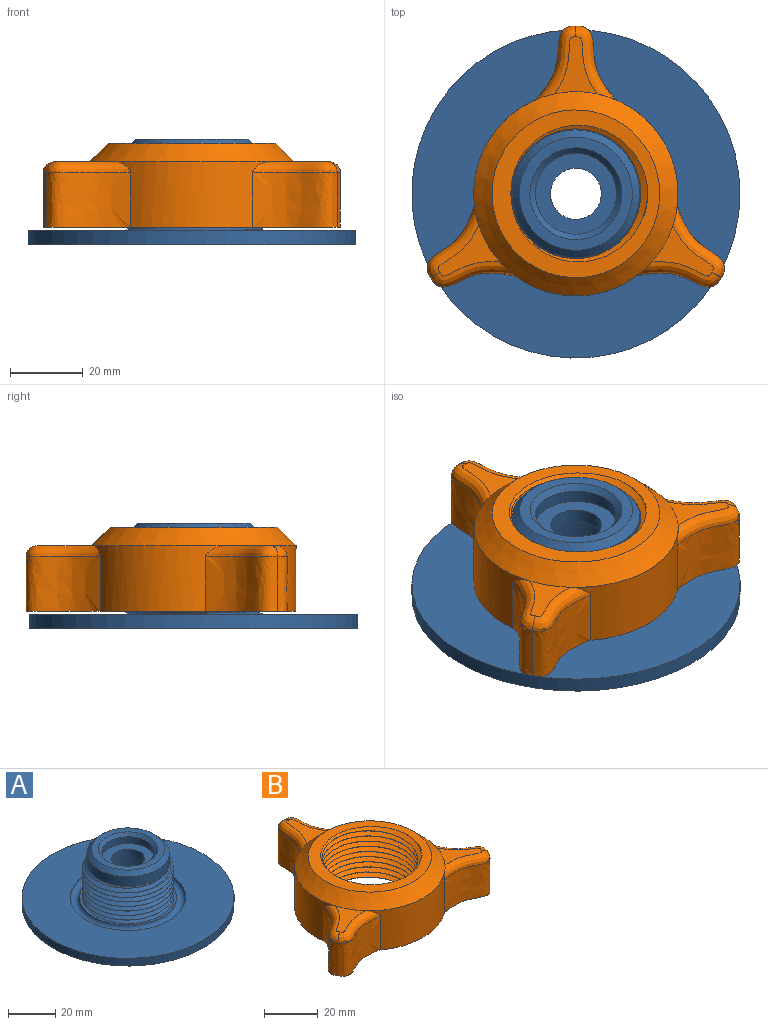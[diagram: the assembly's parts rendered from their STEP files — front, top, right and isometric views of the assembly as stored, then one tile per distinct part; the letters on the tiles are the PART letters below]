
ASSEMBLY  parts=2 mates=1
PART A: 28 faces, bbox 91.3x91.3x30.3 mm
  f0: plane 90x90mm, normal (0,0,1), area 4476mm2, adj f16,f27
  f1: plane 41x41mm, normal (0,0,1), area 137.9mm2, adj f12,f24,f27
  f2: cylinder r=17.5mm len=35mm, axis (0,0,1), area 572.2mm2, adj f9,f11,f22,f23,f25
  f3: cylinder r=17.5mm len=35mm, axis (0,0,1), area 11.5mm2, adj f4,f10,f11,f25,f26
  f4: cylinder r=17.5mm len=35mm, axis (0,0,1), area 11.7mm2, adj f3,f5,f11,f25
  f5: cylinder r=17.5mm len=35mm, axis (0,0,1), area 11.6mm2, adj f4,f6,f11,f25
  f6: cylinder r=17.5mm len=35mm, axis (0,0,1), area 11.7mm2, adj f5,f7,f11,f25
  f7: cylinder r=17.5mm len=35mm, axis (0,0,1), area 11.6mm2, adj f6,f8,f11,f25
  f8: cylinder r=17.5mm len=35mm, axis (0,0,1), area 11.7mm2, adj f7,f9,f11,f25
  f9: cylinder r=17.5mm len=35mm, axis (0,0,1), area 11.7mm2, adj f2,f8,f11,f25
  f10: plane 1.9x1.1mm, normal (0,1,0), area 1.1mm2, adj f3,f12,f24,f25,f26
  f11: bspline ~44.8x38.8mm, area 1936.3mm2, adj f2,f3,f4,f5,f6,f7,f8,f9
  f12: cylinder r=19.4mm len=38.8mm, axis (0,0,-1), area 438.1mm2, adj f1,f10,f11,f22,f25
  f13: plane 31x31mm, normal (0,0,1), area 256mm2, adj f21,f23
  f14: cylinder r=11.1mm len=22.2mm, axis (0,0,-1), area 1394.9mm2, adj f17,f20
  f15: cylinder r=11.1mm len=22.2mm, axis (0,0,-1), area 244.1mm2, adj f19,f21
  f16: cylinder r=45mm len=90mm, axis (0,0,1), area 1131mm2, adj f0,f17
  f17: plane 90x90mm, normal (0,0,-1), area 5974.6mm2, adj f14,f16
  f18: cylinder r=7mm len=14mm, axis (0,0,-1), area 175.9mm2, adj f19,f20
  f19: plane 22.2x22.2mm, normal (0,0,1), area 233.1mm2, adj f15,f18
  f20: plane 22.2x22.2mm, normal (0,0,-1), area 233.1mm2, adj f14,f18
  f21: cone r=11.1mm half-angle=45deg, axis (0,0,1), area 157.9mm2, adj f13,f15
  f22: cone r=17.4mm half-angle=45deg, axis (0,0,-1), area 149.8mm2, adj f2,f11,f12,f25
  f23: cone r=15.5mm half-angle=45deg, axis (0,0,-1), area 293.2mm2, adj f2,f13
  f24: cylinder r=19.4mm len=38.8mm, axis (0,0,-1), area 66.4mm2, adj f1,f10,f11,f26
  f25: bspline ~44.8x38.8mm, area 1858.4mm2, adj f2,f3,f4,f5,f6,f7,f8,f9
  f26: plane 40.13x21.97mm, normal (0,0,1), area 61.7mm2, adj f3,f10,f11,f24
  f27: torus R=22.5mm, axis (0,0,1), area 888.3mm2, adj f0,f1
PART B: 27 faces, bbox 84.7x76x27.2 mm
  f0: plane 83.01x74.27mm, normal (0,0,-1), area 1200.2mm2, adj f2,f3,f8,f10,f11,f13,f14,f16
  f1: plane 42.7x42.7mm, normal (0,0,-1), area 217.3mm2, adj f4,f5,f6,f7,f26
  f2: cylinder r=28mm len=41.7mm, axis (0,0,-1), area 661mm2, adj f0,f14,f16,f19,f21,f22
  f3: cylinder r=28mm len=36.12mm, axis (0,0,-1), area 661mm2, adj f0,f11,f13,f19,f23,f25
  f4: bspline ~45.5x39.4mm, area 2526.4mm2, adj f1,f5,f7,f9
  f5: cylinder r=17.8mm len=35.6mm, axis (0,0,-1), area -15.8mm2, adj f1,f4,f6,f9
  f6: bspline ~45.5x39.4mm, area 2527.5mm2, adj f1,f5,f7,f9
  f7: cylinder r=19.7mm len=39.4mm, axis (0,0,-1), area -4.4mm2, adj f1,f4,f6,f9
  f8: cylinder r=28mm len=36.12mm, axis (0,0,-1), area 661mm2, adj f0,f10,f17,f19,f20,f24
  f9: plane 47.52x47.52mm, normal (0,0,1), area 558.9mm2, adj f4,f5,f6,f7,f19
  f10: extruded ~20.3x15mm, area 375.7mm2, adj f0,f8,f11,f24
  f11: extruded ~20.3x15mm, area 375.7mm2, adj f0,f3,f10,f25
  f12: plane 15.61x11.52mm, normal (0,0,1), area 81.8mm2, adj f19,f24,f25
  f13: extruded ~19.78x15mm, area 375.7mm2, adj f0,f3,f14,f23
  f14: extruded ~23.14x15mm, area 375.7mm2, adj f0,f2,f13,f22
  f15: plane 16.91x13.83mm, normal (0,0,1), area 81.8mm2, adj f19,f22,f23
  f16: extruded ~23.14x15mm, area 375.7mm2, adj f0,f2,f17,f21
  f17: extruded ~19.78x15mm, area 375.7mm2, adj f0,f8,f16,f20
  f18: plane 16.91x13.83mm, normal (0,0,1), area 81.8mm2, adj f19,f20,f21
  f19: cone r=23mm half-angle=45deg, axis (0,0,-1), area 1132.9mm2, adj f2,f3,f8,f9,f12,f15,f18
  f20: bspline ~20.47x15.98mm, area 105.3mm2, adj f8,f17,f18,f21
  f21: bspline ~24.84x6.92mm, area 105.2mm2, adj f2,f16,f18,f20
  f22: bspline ~24.84x6.92mm, area 105.3mm2, adj f2,f14,f15,f23
  f23: bspline ~20.47x15.98mm, area 105.2mm2, adj f3,f13,f15,f22
  f24: bspline ~22.93x11.81mm, area 105.2mm2, adj f8,f10,f12,f25
  f25: bspline ~22.93x11.81mm, area 105.3mm2, adj f3,f11,f12,f24
  f26: torus R=22.5mm, axis (0,0,-1), area 888.3mm2, adj f0,f1
PLACE A t=(1.23,-13.62,-7.5)mm
PLACE B t=(1.23,-13.62,-6.7)mm
MATE fastened A.f14 <-> B.f26  axis (0,0,-1) through (1.23,-13.62,-11.5)mm
